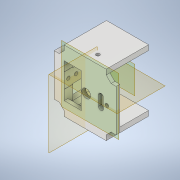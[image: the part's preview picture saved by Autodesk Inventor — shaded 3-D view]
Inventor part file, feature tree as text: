
AUTODESK INVENTOR PART (.ipt)
format: ipt  version: 2022 (Build 260153000, 153)  size: 430,592 bytes
history: native  units: mm
features: extrude x12, sketch x11, reference x9, other x9, plane x8, projected_geometry x3, chamfer x1, pattern_linear x1, hole x1
ambient origin geometry x8: Origin, YZ Plane, XZ Plane, XY Plane, X Axis, Y Axis, Z Axis, Center Point
bodies: Solid1 (feature_tree)
feature tree (55):
  plane  "Work Plane1"
  extrude  "Extrusion1"  Depth=3.0mm
  chamfer  "Chamfer1"  Distance=3.0mm
  sketch  "Sketch2"  dims[d6=3.0mm d7=3.0mm d8=3.0mm d9=0.0mm]
  plane  "Work Plane2"
  extrude  "Extrusion2"  Depth=2.0mm TaperAngle=0.0deg
  sketch  "Sketch4"  dims[d10=3.9mm d11=2.0mm d12=45.0deg d14=31.5mm d15=0.0mm]
  plane  "Work Plane3"
  extrude  "Extrusion4"  Depth=2.0mm
  extrude  "Extrusion5"  Depth=2.8mm
  pattern_linear  "Rectangular Pattern1"  Count1=5 Spacing1=6.25mm
  plane  "Work Plane4"
  hole  "Hole2"  [1 undecoded]
  plane  "Work Plane6"
  plane  "Work Plane5"
  plane  "Work Plane7"
  plane  "Work Plane8"
  extrude  "Extrusion14"  TaperAngle=0.0deg  [1 undecoded]
  extrude  "Extrusion15"  Depth=34.0mm TaperAngle=0.0deg
  extrude  "Extrusion16"  Depth=4.0mm
  extrude  "Extrusion19"  Depth=3.0mm
  extrude  "Extrusion21"  Depth=10.0mm TaperAngle=0.0deg
  extrude  "Extrusion22"  Depth=4.0mm TaperAngle=0.0deg
  extrude  "Extrusion23"  Depth=10.0mm
  extrude  "Extrusion24"  TaperAngle=0.0deg  [1 undecoded]
  projected_geometry  "Projected Loop1"
  reference  "Reference9"
  reference  "Reference10"
  reference  "Reference11"
  sketch  "Sketch12"  dims[d22=7.88mm d23=0.0mm d24=2.0mm]
  reference  "Reference23"
  reference  "Reference32"
  reference  "Reference34"
  reference  "Reference35"
  sketch  "Skizze18"  dims[d25=2.8mm d26=2.8mm]
  projected_geometry  "Projizierte Kontur10"
  sketch  "Skizze19"  dims[d27=10.0mm d28=0.0mm d29=50.0mm d31=6.25mm]
  sketch  "Skizze20"  dims[d56=2.8mm d57=6.0mm d58=6.0mm d59=3.0mm d60=90.0deg d61=8.0mm d62=20.594885mm d86=49.7mm]
  reference  "Referenz44"
  reference  "Referenz45"
  sketch  "Skizze23"  dims[d87=24.85mm d88=0.0mm]
  sketch  "Skizze25"  dims[d100=10.0mm d101=0.0mm d102=34.0mm d103=0.0mm]
  projected_geometry  "Projizierte Kontur14"
  sketch  "Skizze26"  dims[d104=4.0mm d105=4.0mm]
  sketch  "Skizze27"  dims[d106=34.0mm d107=0.0mm d115=3.0mm]
  sketch  "Sketch28"  dims[d118=7.0mm d119=0.5mm d120=0.0mm d129=4.0mm d130=0.0mm d132=2.8mm d133=0.0mm d134=0.0mm d135=4.0mm d136=4.0mm d137=2.8mm d138=0.0mm d139=0.0mm d140=8.0mm d142=7.0mm d143=3.8mm d144=10.0mm d145=0.0mm d116=0.872665mm d117=0.5mm]
  other  "Assembly_Cube_Z_Focus_MGN_NEMA_v3.iam"
  other  "00_MGN12 LINEAR GUIDE RAIL, CONFIGURABLE:1"
  other  "Assembly_Cube_empty_IM_v3:1"
  other  "10_Cube_1x1_IM:1"
  other  "Assembly_Cube_empty_IM_v3:2"
  other  "10_Cube_1x1_IM:2"
  other  "30_Cube_Z_Focus_MGN_NEMA_Motoradapter_NEMA11_v3:1"
  other  "Assembly_Cube_Z_Focus_MGN_NEMA_belt_pushing_v3.iam"
  other  "00_MGN12H, LINEAR GUIDE BLOCK:1"
note: 3 required parameter values undecoded (feature->parameter linkage not recoverable at this tier; creation-order binding heuristic only, values carry confidence <= 0.55)
